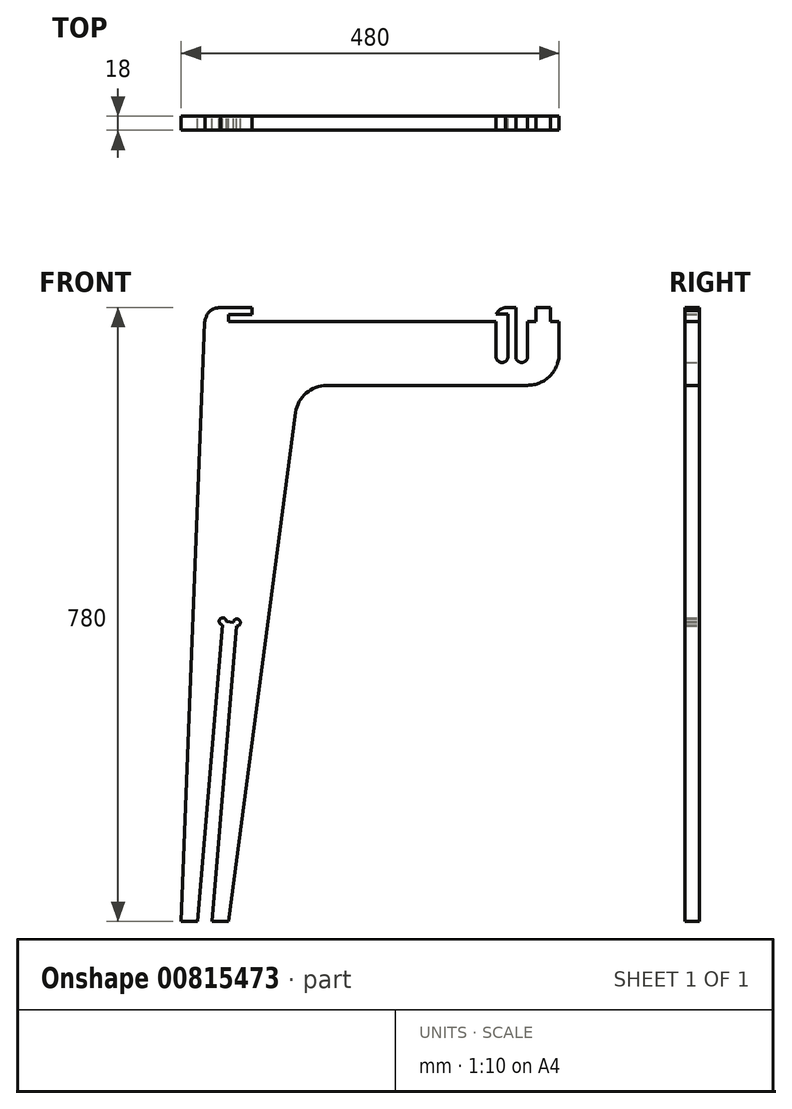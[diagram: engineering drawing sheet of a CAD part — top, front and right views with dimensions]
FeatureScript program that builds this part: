
annotation { "Feature Type Name" : "Feature", "Feature Type Description" : "" }
export const myFeature = defineFeature(function(context is Context, id is Id, definition is map)
    precondition{}
    {
        {
            var Q0;
            Q0=qCreatedBy(makeId("Front.planeOp"),FACE);
            var sketch = newSketch(context, id + "F0", { "sketchPlane" : qUnion([Q0])});
            skLineSegment(sketch, "E0.top", {"start": v(-495.34, -390.31) * mm, "end": v(-474.4, -390.31) * mm});
            skLineSegment(sketch, "E0.right", {"start": v(-15.4, 371.5) * mm, "end": v(-15.34, 330.81) * mm});
            skPoint(sketch, "E0.middle", {"position": v(-255.39, -0.31) * mm});
            skLineSegment(sketch, "E1", {"start": v(-495.34, -390.31) * mm, "end": v(-465.4, 370.31) * mm});
            skLineSegment(sketch, "E2.trimOffspring", {"start": v(-445.34, 389.69) * mm, "end": v(-405.34, 389.69) * mm});
            skPoint(sketch, "E3.left.start.orphan", {"position": v(-496.63, 389.69) * mm});
            skLineSegment(sketch, "E4.right", {"start": v(-435.34, 376.19) * mm, "end": v(-435.34, 375.19) * mm});
            skLineSegment(sketch, "E5.bottom", {"start": v(-435.34, 380.69) * mm, "end": v(-405.34, 380.69) * mm});
            skLineSegment(sketch, "E5.right", {"start": v(-405.34, 380.69) * mm, "end": v(-405.34, 389.69) * mm});
            skFitSpline(sketch, "E6", {"points": [v(-445.34, 389.69) * mm, v(-458.05, 385.65) * mm, v(-465.32, 372.69) * mm], "startDerivative": vector(-30.02, -3.87) * mm, "endDerivative": vector(-10.34, -33.58) * mm});
            skLineSegment(sketch, "E7.top", {"start": v(-495.34, -380.32) * mm, "end": v(-494.94, -380.32) * mm});
            skLineSegment(sketch, "E8", {"start": v(-435.34, 380.69) * mm, "end": v(-435.34, 371.69) * mm});
            skLineSegment(sketch, "E9", {"start": v(-349.93, 255.99) * mm, "end": v(-435.34, -390.31) * mm});
            skLineSegment(sketch, "E10", {"start": v(-310.27, 290.75) * mm, "end": v(-55.34, 290.75) * mm});
            skPoint(sketch, "E11.orphan", {"position": v(-14.14, -390.31) * mm});
            skPoint(sketch, "E12.visualSharp", {"position": v(-345.34, 290.75) * mm});
            skArc(sketch, "E12.filletArc", {"start": v(-310.27, 290.75) * mm, "mid": v(-336.64, 280.83) * mm, "end": v(-349.93, 255.99) * mm});
            skPoint(sketch, "E13.visualSharp", {"position": v(-15.27, 290.75) * mm});
            skArc(sketch, "E13.filletArc", {"start": v(-55.34, 290.75) * mm, "mid": v(-27.03, 302.49) * mm, "end": v(-15.34, 330.81) * mm});
            skLineSegment(sketch, "E14", {"start": v(-95.34, 381.2) * mm, "end": v(-80.34, 381.23) * mm});
            skLineSegment(sketch, "E15", {"start": v(-55.34, 327.19) * mm, "end": v(-55.34, 371.5) * mm});
            skLineSegment(sketch, "E16.top", {"start": v(-62.84, 319.69) * mm, "end": v(-62.84, 319.69) * mm});
            skLineSegment(sketch, "E16.left", {"start": v(-55.34, 371.5) * mm, "end": v(-55.34, 327.19) * mm});
            skLineSegment(sketch, "E16.right", {"start": v(-70.34, 389.69) * mm, "end": v(-70.34, 327.19) * mm});
            skLineSegment(sketch, "E17.right", {"start": v(-80.34, 381.23) * mm, "end": v(-80.34, 327.19) * mm});
            skLineSegment(sketch, "E18.top", {"start": v(-87.84, 319.69) * mm, "end": v(-87.84, 319.69) * mm});
            skLineSegment(sketch, "E18.right", {"start": v(-95.34, 370.69) * mm, "end": v(-95.34, 327.19) * mm});
            skPoint(sketch, "E19.visualSharp", {"position": v(-80.34, 388.1) * mm});
            skPoint(sketch, "E20.visualSharp", {"position": v(-95.34, 389.69) * mm});
            skPoint(sketch, "E21.visualSharp", {"position": v(-70.34, 319.69) * mm});
            skArc(sketch, "E21.filletArc", {"start": v(-70.34, 327.19) * mm, "mid": v(-68.14, 321.89) * mm, "end": v(-62.84, 319.69) * mm});
            skPoint(sketch, "E22.visualSharp", {"position": v(-55.34, 319.69) * mm});
            skArc(sketch, "E22.filletArc", {"start": v(-62.84, 319.69) * mm, "mid": v(-57.53, 321.89) * mm, "end": v(-55.34, 327.19) * mm});
            skPoint(sketch, "E23.visualSharp", {"position": v(-80.34, 319.69) * mm});
            skArc(sketch, "E23.filletArc", {"start": v(-87.84, 319.69) * mm, "mid": v(-82.53, 321.89) * mm, "end": v(-80.34, 327.19) * mm});
            skPoint(sketch, "E24.visualSharp", {"position": v(-95.34, 319.69) * mm});
            skArc(sketch, "E24.filletArc", {"start": v(-95.34, 327.19) * mm, "mid": v(-93.14, 321.89) * mm, "end": v(-87.84, 319.69) * mm});
            skLineSegment(sketch, "E25.trimOffspring", {"start": v(-44.49, 389.69) * mm, "end": v(-26.47, 389.69) * mm});
            skLineSegment(sketch, "E26.trimOffspring", {"start": v(-83.34, 389.69) * mm, "end": v(-70.34, 389.69) * mm});
            skPoint(sketch, "E27.trimOffspring.end.orphan", {"position": v(-15.43, 380.69) * mm});
            skLineSegment(sketch, "E28", {"start": v(-465.32, 372.69) * mm, "end": v(-465.4, 370.31) * mm});
            skLineSegment(sketch, "E29", {"start": v(-95.34, 389.69) * mm, "end": v(-83.34, 389.69) * mm});
            skLineSegment(sketch, "E30", {"start": v(-435.34, 371.69) * mm, "end": v(-95.34, 371.69) * mm});
            skLineSegment(sketch, "E31", {"start": v(-95.34, 370.69) * mm, "end": v(-95.34, 371.69) * mm});
            skLineSegment(sketch, "E32", {"start": v(-26.46, 385.82) * mm, "end": v(-26.19, 371.5) * mm});
            skLineSegment(sketch, "E33", {"start": v(-26.46, 385.82) * mm, "end": v(-26.47, 389.69) * mm});
            skLineSegment(sketch, "E34.trimOffspring", {"start": v(-55.34, 371.5) * mm, "end": v(-44.49, 371.5) * mm});
            skPoint(sketch, "E35.orphan", {"position": v(-15.43, 389.69) * mm});
            skLineSegment(sketch, "E36.trimOffspring", {"start": v(-26.19, 371.5) * mm, "end": v(-15.4, 371.5) * mm});
            skLineSegment(sketch, "E37", {"start": v(-44.49, 389.69) * mm, "end": v(-44.49, 371.5) * mm});
            skFitSpline(sketch, "E38", {"points": [v(-83.34, 389.69) * mm, v(-90.78, 386.65) * mm, v(-95.34, 381.2) * mm], "startDerivative": vector(-15.74, -4.53) * mm, "endDerivative": vector(-8.18, -12.53) * mm});
            skLineSegment(sketch, "E39", {"start": v(-456.34, -390.31) * mm, "end": v(-424.6, -10.64) * mm});
            skPoint(sketch, "E39.endSnap0", {"position": v(-392.63, -67.16) * mm});
            skLineSegment(sketch, "E40", {"start": v(-429.08, -10.26) * mm, "end": v(-438.05, -9.51) * mm});
            skLineSegment(sketch, "E41", {"start": v(-442.9, -13.62) * mm, "end": v(-474.4, -390.31) * mm});
            skLineSegment(sketch, "E42.trimOffspring", {"start": v(-456.34, -390.31) * mm, "end": v(-435.34, -390.31) * mm});
            skPoint(sketch, "E43.end.orphan", {"position": v(-495.34, -413.97) * mm});
            skPoint(sketch, "E43.start.orphan", {"position": v(-495.34, -402.14) * mm});
            skPoint(sketch, "E44.end.orphan", {"position": v(-456.34, -401.66) * mm});
            skPoint(sketch, "E45.orphan", {"position": v(-392.63, 371.69) * mm});
            skArc(sketch, "E46", {"start": v(-438.05, -9.51) * mm, "mid": v(-445.44, -5.7) * mm, "end": v(-442.9, -13.62) * mm});
            skArc(sketch, "E47", {"start": v(-424.97, -15.12) * mm, "mid": v(-421.16, -7.73) * mm, "end": v(-429.08, -10.26) * mm});
            skSolve(sketch);
        }
        {
            var Q0;
            Q0=makeQuery(id+"F0.imprint","IMPRINT",FACE,{"disambiguationData":[TD([[makeQuery(id+"F0.imprint","IMPRINT",EDGE,{"derivedFrom":sQuery(id+"F0.wireOp",EDGE,"E0.right")}),-1.0]])]});
            extrude(context, id + "F1", {"entities" : qUnion([Q0]), "depth" : 18 * mm, "offsetDistance" : 25 * mm});
        }
    });
